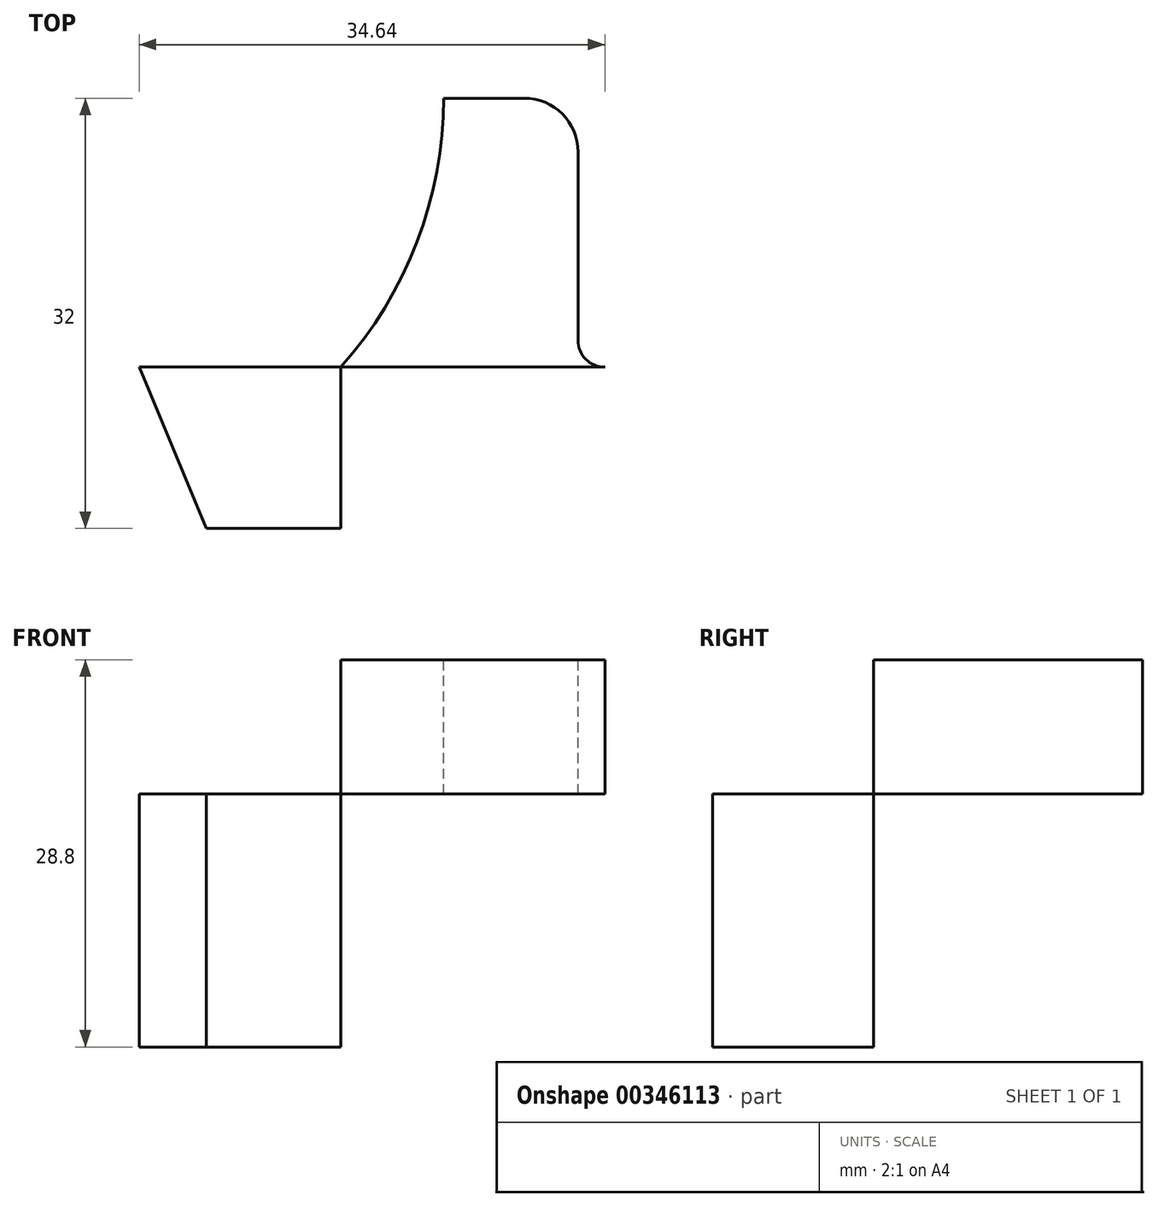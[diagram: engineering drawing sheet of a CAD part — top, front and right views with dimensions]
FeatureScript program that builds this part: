
annotation { "Feature Type Name" : "Feature", "Feature Type Description" : "" }
export const myFeature = defineFeature(function(context is Context, id is Id, definition is map)
    precondition{}
    {
        {
            var Q0;
            Q0=qCreatedBy(makeId("Top.planeOp"),FACE);
            var sketch = newSketch(context, id + "F0", { "sketchPlane" : qUnion([Q0])});
            skLineSegment(sketch, "E0", {"start": v(0, -12) * mm, "end": v(200, -12) * mm});
            skLineSegment(sketch, "E1", {"start": v(200, -12) * mm, "end": v(200, -4) * mm});
            skLineSegment(sketch, "E2", {"start": v(196, 0) * mm, "end": v(77, 0) * mm});
            skLineSegment(sketch, "E3", {"start": v(75, 2) * mm, "end": v(75, 16) * mm});
            skLineSegment(sketch, "E4", {"start": v(71, 20) * mm, "end": v(65, 20) * mm});
            skLineSegment(sketch, "E5", {"start": v(0, -12) * mm, "end": v(57.36, -12) * mm});
            skLineSegment(sketch, "E6", {"start": v(57.36, -12) * mm, "end": v(57.36, 0) * mm});
            skArc(sketch, "E7", {"start": v(57.36, 0) * mm, "mid": v(63.02, 9.3) * mm, "end": v(65, 20) * mm});
            skArc(sketch, "E8", {"start": v(0, -12) * mm, "mid": v(-9.07, 7.86) * mm, "end": v(11.88, 1.71) * mm});
            skLineSegment(sketch, "E9", {"start": v(0, -12) * mm, "end": v(47.36, -12) * mm, "construction": true});
            skLineSegment(sketch, "E10", {"start": v(47.36, -12) * mm, "end": v(42.36, -12) * mm, "construction": true});
            skLineSegment(sketch, "E11", {"start": v(42.36, 0) * mm, "end": v(47.36, -12) * mm});
            skLineSegment(sketch, "E12", {"start": v(13.86, 0) * mm, "end": v(42.36, 0) * mm});
            skLineSegment(sketch, "E13", {"start": v(42.36, 0) * mm, "end": v(57.36, 0) * mm});
            skCircle(sketch, "E14", {"center": v(0, 0) * mm, "radius": 7 * mm});
            skPoint(sketch, "E15.visualSharp", {"position": v(75, 20) * mm});
            skArc(sketch, "E15.filletArc", {"start": v(75, 16) * mm, "mid": v(73.83, 18.83) * mm, "end": v(71, 20) * mm});
            skPoint(sketch, "E16.visualSharp", {"position": v(200, 0) * mm});
            skArc(sketch, "E16.filletArc", {"start": v(200, -4) * mm, "mid": v(198.83, -1.17) * mm, "end": v(196, 0) * mm});
            skPoint(sketch, "E17.visualSharp", {"position": v(12, 0) * mm});
            skArc(sketch, "E17.filletArc", {"start": v(11.88, 1.71) * mm, "mid": v(12.55, 0.49) * mm, "end": v(13.86, 0) * mm});
            skPoint(sketch, "E18.visualSharp", {"position": v(75, 0) * mm});
            skArc(sketch, "E18.filletArc", {"start": v(75, 2) * mm, "mid": v(75.59, 0.59) * mm, "end": v(77, 0) * mm});
            skLineSegment(sketch, "E19", {"start": v(77, 0) * mm, "end": v(57.36, 0) * mm});
            skSolve(sketch);
        }
        {
            var Q0;
            Q0=makeQuery(id+"F0.imprint","IMPRINT",FACE,{"disambiguationData":[TD([[makeQuery(id+"F0.imprint","IMPRINT",EDGE,{"derivedFrom":sQuery(id+"F0.wireOp",EDGE,"E0")}),1.0]])]});
            var Q1;
            {var subQ0=sQuery(id+"F0.wireOp",EDGE,"E8");Q1=makeQuery(id+"F0.imprint","IMPRINT",FACE,{"disambiguationData":[TD([[makeQuery(id+"F0.imprint","IMPRINT",EDGE,{"derivedFrom":subQ0}),-1.0]])]});}
            var Q2;
            {var subQ0=sQuery(id+"F0.wireOp",EDGE,"E6");Q2=makeQuery(id+"F0.imprint","IMPRINT",FACE,{"disambiguationData":[TD([[makeQuery(id+"F0.imprint","IMPRINT",EDGE,{"derivedFrom":subQ0}),1.0]])]});}
            extrude(context, id + "F1", {"entities" : qUnion([Q0, Q1, Q2]), "oppositeDirection" : true, "depth" : 28.8 * mm});
        }
        {
            var Q0;
            Q0=makeQuery(id+"F0.imprint","IMPRINT",FACE,{"disambiguationData":[TD([[makeQuery(id+"F0.imprint","IMPRINT",EDGE,{"derivedFrom":sQuery(id+"F0.wireOp",EDGE,"E3")}),1.0]])]});
            extrude(context, id + "F2", {"entities" : qUnion([Q0]), "operationType" : NewBodyOperationType.ADD, "oppositeDirection" : true, "depth" : 10 * mm});
        }
        {
            var Q0;
            {var subQ0=sQuery(id+"F0.wireOp",EDGE,"E6");Q0=makeQuery(id+"F0.imprint","IMPRINT",FACE,{"disambiguationData":[TD([[makeQuery(id+"F0.imprint","IMPRINT",EDGE,{"derivedFrom":subQ0}),1.0]])]});}
            extrude(context, id + "F3", {"entities" : qUnion([Q0]), "operationType" : NewBodyOperationType.REMOVE, "oppositeDirection" : true, "depth" : 10 * mm});
        }
        {
            var Q0;
            Q0=makeQuery(id+"F1.opExtrude","SWEPT_FACE",FACE,{"disambiguationData":[OSD([sQuery(id+"F0.wireOp",EDGE,"E0"),sQuery(id+"F0.wireOp",EDGE,"E5")])]});
            var sketch = newSketch(context, id + "F4", { "sketchPlane" : qUnion([Q0])});
            skCircle(sketch, "E20", {"center": v(177, -19.4) * mm, "radius": 3.9 * mm});
            skSolve(sketch);
        }
        {
            var Q0;
            Q0 = qSketchRegion(id + "F4", true);
            extrude(context, id + "F5", {"entities" : qUnion([Q0]), "operationType" : NewBodyOperationType.REMOVE, "endBound" : BoundingType.THROUGH_ALL, "oppositeDirection" : true, "depth" : 25 * mm});
        }
        {
            var Q0;
            Q0=qCreatedBy(makeId("Front.planeOp"),FACE);
            var sketch = newSketch(context, id + "F6", { "sketchPlane" : qUnion([Q0])});
            skLineSegment(sketch, "E21.bottom", {"start": v(-15.77, -20.4) * mm, "end": v(14.23, -20.4) * mm});
            skLineSegment(sketch, "E21.top", {"start": v(-15.77, -8.4) * mm, "end": v(14.23, -8.4) * mm});
            skLineSegment(sketch, "E21.left", {"start": v(-15.77, -20.4) * mm, "end": v(-15.77, -8.4) * mm});
            skLineSegment(sketch, "E21.right", {"start": v(14.23, -20.4) * mm, "end": v(14.23, -8.4) * mm});
            skSolve(sketch);
        }
        {
            var Q0;
            Q0 = qSketchRegion(id + "F6", true);
            extrude(context, id + "F7", {"entities" : qUnion([Q0]), "operationType" : NewBodyOperationType.REMOVE, "endBound" : BoundingType.SYMMETRIC, "oppositeDirection" : true, "depth" : 100 * mm});
        }
    });
